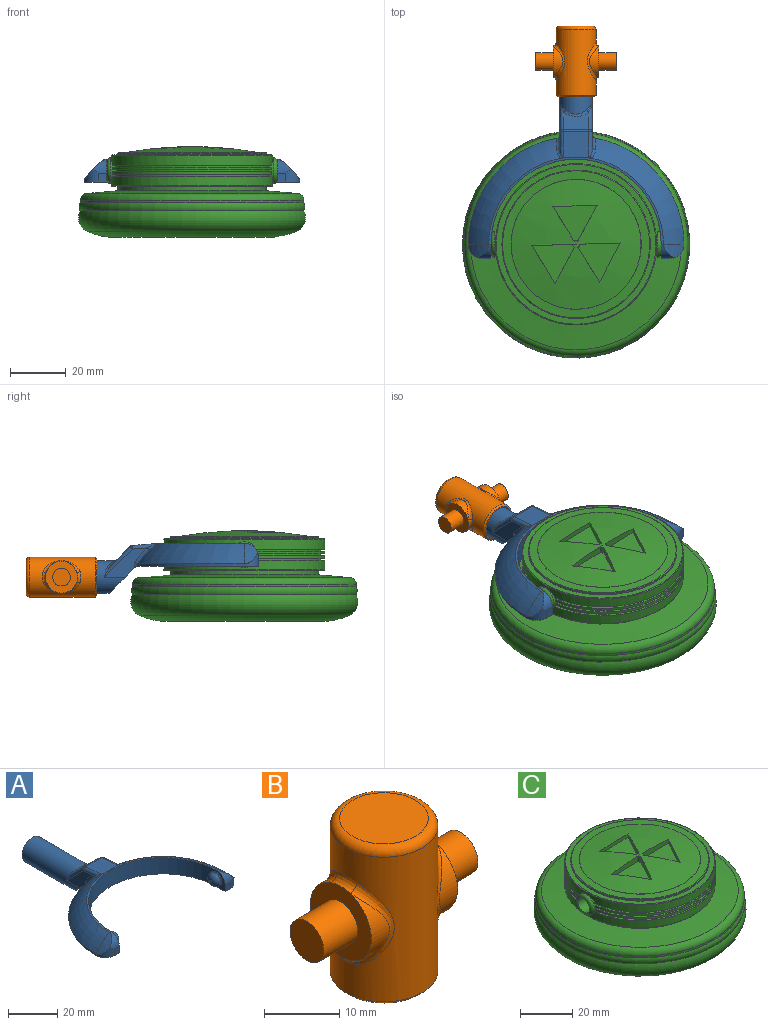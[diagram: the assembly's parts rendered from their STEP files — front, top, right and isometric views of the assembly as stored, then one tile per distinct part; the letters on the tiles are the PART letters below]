
ASSEMBLY  parts=3 mates=2
PART A: 48 faces, bbox 77.3x80.8x18.2 mm
  f0: plane 11.99x9.83mm, normal (0,-0.71,-0.71), area 141.5mm2, adj f1,f2,f9,f30,f43,f46
  f1: plane 15.39x10.49mm, normal (-1,0,0), area 63.5mm2, adj f0,f30,f32,f36,f46,f47
  f2: plane 15.39x10.49mm, normal (1,0,0), area 63.5mm2, adj f0,f30,f34,f39,f43,f44
  f3: plane 9.14x6.37mm, normal (0,0.71,0.71), area 67.6mm2, adj f35,f36,f39,f40
  f4: cylinder r=38.61mm len=37.99mm, axis (0,0,-1), area 42.6mm2, adj f6,f9,f17,f46,f47
  f5: torus R=19.3mm, axis (0,0,-1), area 507.8mm2, adj f10,f11,f12,f29,f42,f44
  f6: torus R=19.3mm, axis (0,0,-1), area 507.8mm2, adj f4,f11,f15,f28,f45,f47
  f7: cylinder r=30.48mm len=60.96mm, axis (0,0,-1), area 746.6mm2, adj f8,f9,f11,f14,f21,f24
  f8: plane 8.13x5.08mm, normal (-1,0,0), area 19.9mm2, adj f7,f9,f13,f19,f24
  f9: plane 77.22x43.73mm, normal (0,0,-1), area 956.2mm2, adj f0,f4,f7,f8,f10,f13,f14,f16
  f10: cylinder r=38.61mm len=37.99mm, axis (0,0,-1), area 42.6mm2, adj f5,f9,f20,f43,f44
  f11: plane 62.55x30.95mm, normal (0,0,1), area 75mm2, adj f5,f6,f7,f18,f19,f27
  f12: cylinder r=22.71mm len=7.33mm, axis (0,1,0), area 24.8mm2, adj f5,f19,f20
  f13: plane 3.05x3.05mm, normal (0,-1,0), area 9.3mm2, adj f8,f9,f19,f20
  f14: plane 8.13x5.08mm, normal (1,0,0), area 19.9mm2, adj f7,f9,f16,f18,f21
  f15: cylinder r=22.71mm len=7.33mm, axis (0,1,0), area 24.8mm2, adj f6,f17,f18
  f16: plane 3.05x3.05mm, normal (0,-1,0), area 9.3mm2, adj f9,f14,f17,f18
  f17: cylinder r=5.08mm len=5.08mm, axis (0,0,-1), area 21.9mm2, adj f4,f9,f15,f16,f18
  f18: cylinder r=5.08mm len=5.08mm, axis (-1,0,0), area 21.9mm2, adj f11,f14,f15,f16,f17
  f19: cylinder r=5.08mm len=5.08mm, axis (-1,0,0), area 21.9mm2, adj f8,f11,f12,f13,f20
  f20: cylinder r=5.08mm len=5.08mm, axis (0,0,-1), area 21.9mm2, adj f9,f10,f12,f13,f19
  f21: cylinder r=3.17mm len=6.35mm, axis (-1,0,0), area 12.7mm2, adj f7,f14,f23
  f22: plane 1.27x1.27mm, normal (1,0,0), area 1.3mm2, adj f23
  f23: torus R=0.64mm, axis (1,0,0), area 56.5mm2, adj f21,f22
  f24: cylinder r=3.17mm len=6.35mm, axis (1,0,0), area 12.7mm2, adj f7,f8,f26
  f25: plane 1.27x1.27mm, normal (-1,0,0), area 1.3mm2, adj f26
  f26: torus R=0.64mm, axis (-1,0,0), area 56.5mm2, adj f24,f25
  f27: plane 9.86x9.36mm, normal (0,0.09,1), area 85.6mm2, adj f11,f28,f29,f32,f34,f35,f42,f45
  f28: plane 1.04x0.17mm, normal (0,-1,0), area 0mm2, adj f6,f27,f45
  f29: plane 1.04x0.17mm, normal (0,-1,0), area 0mm2, adj f5,f27,f42
  f30: cylinder r=5.84mm len=33.01mm, axis (0,-1,0), area 1029.7mm2, adj f0,f1,f2,f31,f38,f40,f41
  f31: plane 11.68x11.68mm, normal (0,1,0), area 107.2mm2, adj f30
  f32: cylinder r=1.27mm len=9.13mm, axis (0,-1,0.09), area 14.4mm2, adj f1,f27,f33,f45
  f33: sphere r=1.27mm, area 1.5mm2, adj f32,f35,f36
  f34: cylinder r=1.27mm len=9.13mm, axis (0,1,-0.09), area 14.4mm2, adj f2,f27,f37,f42
  f35: cylinder r=1.27mm len=9.14mm, axis (-1,0,0), area 8.1mm2, adj f3,f27,f33,f37
  f36: cylinder r=1.27mm len=10.91mm, axis (0,-0.71,0.71), area 23.1mm2, adj f1,f3,f33,f38
  f37: sphere r=1.27mm, area 1.5mm2, adj f34,f35,f39
  f38: bspline ~4.55x2.75mm, area 2.3mm2, adj f30,f36,f40
  f39: cylinder r=1.27mm len=10.91mm, axis (0,0.71,-0.71), area 23.1mm2, adj f2,f3,f37,f41
  f40: bspline ~9.14x2.56mm, area 10.7mm2, adj f3,f30,f38,f41
  f41: bspline ~5.23x3.53mm, area 2.3mm2, adj f30,f39,f40
  f42: bspline ~4.62x3.14mm, area 5.2mm2, adj f5,f27,f29,f34,f44
  f43: cylinder r=1.27mm len=1.74mm, axis (0,0,-1), area 1.9mm2, adj f0,f2,f9,f10,f44
  f44: bspline ~8.6x7.86mm, area 11.9mm2, adj f2,f5,f10,f42,f43
  f45: bspline ~4.62x3.14mm, area 5.2mm2, adj f6,f27,f28,f32,f47
  f46: cylinder r=1.27mm len=1.74mm, axis (0,0,-1), area 1.9mm2, adj f0,f1,f4,f9,f47
  f47: bspline ~8.6x7.86mm, area 11.9mm2, adj f1,f4,f6,f45,f46
PART B: 25 faces, bbox 28.9x15.5x25.4 mm
  f0: cylinder r=5.71mm len=10.81mm, axis (-1,0,0), area 26.2mm2, adj f5,f15
  f1: cylinder r=5.71mm len=10.81mm, axis (-1,0,0), area 26.2mm2, adj f8,f11
  f2: cylinder r=7.14mm len=23.5mm, axis (0,0,-1), area 763.2mm2, adj f9,f10,f11,f12,f13,f14,f15,f16
  f3: plane 11.75x11.75mm, normal (0,0,1), area 108.4mm2, adj f17
  f4: plane 13.02x13.02mm, normal (0,0,-1), area 16.3mm2, adj f22,f24
  f5: plane 11.46x11.46mm, normal (1,0,0), area 70.9mm2, adj f0,f6,f13,f16,f18
  f6: cylinder r=5.71mm len=10.81mm, axis (-1,0,0), area 26.2mm2, adj f5,f14
  f7: cylinder r=5.71mm len=10.81mm, axis (-1,0,0), area 26.2mm2, adj f8,f10
  f8: plane 11.46x11.46mm, normal (-1,0,0), area 70.9mm2, adj f1,f7,f9,f12,f20
  f9: bspline ~4.64x1.73mm, area 6.5mm2, adj f2,f8,f10,f11
  f10: bspline ~13.62x4.91mm, area 20.7mm2, adj f2,f7,f9,f12
  f11: bspline ~13.6x4.87mm, area 20.7mm2, adj f1,f2,f9,f12
  f12: bspline ~4.64x1.73mm, area 6.5mm2, adj f2,f8,f10,f11
  f13: bspline ~4.64x1.73mm, area 6.5mm2, adj f2,f5,f14,f15
  f14: bspline ~13.62x4.91mm, area 20.7mm2, adj f2,f6,f13,f16
  f15: bspline ~13.6x4.87mm, area 20.7mm2, adj f0,f2,f13,f16
  f16: bspline ~4.64x1.73mm, area 6.5mm2, adj f2,f5,f14,f15
  f17: torus R=5.87mm, axis (0,0,1), area 83.8mm2, adj f2,f3
  f18: cylinder r=3.17mm len=6.35mm, axis (-1,0,0), area 126.7mm2, adj f5,f19
  f19: plane 6.35x6.35mm, normal (1,0,0), area 31.7mm2, adj f18
  f20: cylinder r=3.17mm len=6.35mm, axis (1,0,0), area 126.7mm2, adj f8,f21
  f21: plane 6.35x6.35mm, normal (-1,0,0), area 31.7mm2, adj f20
  f22: cylinder r=6.1mm len=22.86mm, axis (0,0,-1), area 875.6mm2, adj f4,f23
  f23: plane 12.19x12.19mm, normal (0,0,-1), area 116.7mm2, adj f22
  f24: cone r=7.14mm half-angle=45deg, axis (0,0,1), area 38.5mm2, adj f2,f4
PART C: 64 faces, bbox 96.2x96.2x32.5 mm
  f0: cylinder r=28.87mm len=57.73mm, axis (0,0,-1), area 595.6mm2, adj f1,f2,f54,f55,f60
  f1: plane 57.13x24.71mm, normal (0,0,1), area 102.9mm2, adj f0,f3,f54,f55
  f2: plane 57.13x24.71mm, normal (0,0,1), area 102.9mm2, adj f0,f4,f54,f55
  f3: cylinder r=27.59mm len=54.54mm, axis (0,0,-1), area 49.6mm2, adj f1,f6,f54,f55
  f4: cylinder r=27.59mm len=54.54mm, axis (0,0,-1), area 49.6mm2, adj f2,f5,f54,f55
  f5: plane 57.06x24.48mm, normal (0,0,-1), area 102.3mm2, adj f4,f8,f54,f55
  f6: plane 57.06x24.48mm, normal (0,0,-1), area 102.3mm2, adj f3,f7,f54,f55
  f7: cylinder r=28.87mm len=57.06mm, axis (0,0,-1), area 77.8mm2, adj f6,f11,f54,f55
  f8: cylinder r=28.87mm len=57.06mm, axis (0,0,-1), area 77.8mm2, adj f5,f12,f54,f55
  f9: plane 57.01x24.31mm, normal (0,0,-1), area 101.8mm2, adj f14,f16,f54,f55
  f10: plane 57.01x24.31mm, normal (0,0,-1), area 101.8mm2, adj f13,f15,f54,f55
  f11: plane 57.01x24.31mm, normal (0,0,1), area 101.8mm2, adj f7,f13,f54,f55
  f12: plane 57.01x24.31mm, normal (0,0,1), area 101.8mm2, adj f8,f14,f54,f55
  f13: cylinder r=27.59mm len=54.41mm, axis (0,0,-1), area 49.2mm2, adj f10,f11,f54,f55
  f14: cylinder r=27.59mm len=54.41mm, axis (0,0,-1), area 49.2mm2, adj f9,f12,f54,f55
  f15: cylinder r=28.87mm len=57.06mm, axis (0,0,-1), area 77.9mm2, adj f10,f19,f54,f55
  f16: cylinder r=28.87mm len=57.06mm, axis (0,0,-1), area 77.9mm2, adj f9,f20,f54,f55
  f17: plane 57.13x24.71mm, normal (0,0,-1), area 102.9mm2, adj f22,f23,f54,f55
  f18: plane 57.13x24.71mm, normal (0,0,-1), area 102.9mm2, adj f21,f23,f54,f55
  f19: plane 57.06x24.48mm, normal (0,0,1), area 102.3mm2, adj f15,f21,f54,f55
  f20: plane 57.06x24.48mm, normal (0,0,1), area 102.3mm2, adj f16,f22,f54,f55
  f21: cylinder r=27.59mm len=54.54mm, axis (0,0,-1), area 49.6mm2, adj f18,f19,f54,f55
  f22: cylinder r=27.59mm len=54.54mm, axis (0,0,-1), area 49.6mm2, adj f17,f20,f54,f55
  f23: cylinder r=28.87mm len=57.73mm, axis (0,0,-1), area 595.8mm2, adj f17,f18,f54,f55,f61
  f24: sphere r=135.39mm, area 1385.3mm2, adj f38,f39,f40,f41,f43,f44,f45,f46
  f25: plane 39.33x39.33mm, normal (0,0,-1), area 1214.6mm2, adj f26
  f26: torus R=20.12mm, axis (0,0,-1), area 1429.3mm2, adj f25,f27
  f27: torus R=27.74mm, axis (0,0,-1), area 3542.1mm2, adj f26,f28
  f28: torus R=35.36mm, axis (0,0,-1), area 2180.1mm2, adj f27,f29
  f29: torus R=37.35mm, axis (0,0,-1), area 734.6mm2, adj f28,f30
  f30: cylinder r=40.06mm len=80.11mm, axis (0,0,-1), area 213.3mm2, adj f29,f34
  f31: cone r=26.57mm half-angle=85deg, axis (0,0,-1), area 2265mm2, adj f32,f34
  f32: cylinder r=26.57mm len=53.14mm, axis (0,0,-1), area 265mm2, adj f31,f33
  f33: plane 57.23x57.23mm, normal (0,0,-1), area 354.5mm2, adj f32,f60
  f34: torus R=37.52mm, axis (0,0,1), area 928.6mm2, adj f30,f31
  f35: cone r=26.57mm half-angle=87deg, axis (0,0,-1), area 475.4mm2, adj f62,f63
  f36: cylinder r=26.57mm len=53.14mm, axis (0,0,-1), area 92.3mm2, adj f37,f62
  f37: plane 57.23x57.23mm, normal (0,0,1), area 354.5mm2, adj f36,f61
  f38: cylinder r=1.27mm len=2.53mm, axis (0,0,1), area 3.4mm2, adj f24,f39,f41,f42
  f39: plane 12.43x7.68mm, normal (0.85,0.53,0), area 32.2mm2, adj f24,f38,f40,f42
  f40: plane 13.98x7.52mm, normal (-0.88,0.47,0), area 28mm2, adj f24,f39,f41,f42
  f41: plane 14.6x2.53mm, normal (0.03,-1,0), area 32.2mm2, adj f24,f38,f40,f42
  f42: plane 15.2x13.98mm, normal (0,0,1), area 108.3mm2, adj f38,f39,f40,f41
  f43: plane 12.86x6.92mm, normal (-0.88,0.47,0), area 32.2mm2, adj f24,f44,f46,f47
  f44: cylinder r=1.27mm len=2.53mm, axis (0,0,1), area 3.4mm2, adj f24,f43,f45,f47
  f45: plane 14.6x2.53mm, normal (0.03,-1,0), area 32.2mm2, adj f24,f44,f46,f47
  f46: plane 13.51x8.34mm, normal (0.85,0.53,0), area 28mm2, adj f24,f43,f45,f47
  f47: plane 15.27x13.94mm, normal (0,0,1), area 108.3mm2, adj f43,f44,f45,f46
  f48: cylinder r=1.27mm len=2.53mm, axis (0,0,1), area 3.4mm2, adj f24,f49,f51,f52
  f49: plane 12.86x6.92mm, normal (-0.88,0.47,0), area 32.2mm2, adj f24,f48,f50,f52
  f50: plane 15.87x1.84mm, normal (0.03,-1,0), area 28mm2, adj f24,f49,f51,f52
  f51: plane 12.43x7.68mm, normal (0.85,0.53,0), area 32.2mm2, adj f24,f48,f50,f52
  f52: plane 15.87x12.9mm, normal (0,0,1), area 108.3mm2, adj f48,f49,f50,f51
  f53: plane 6.6x6.6mm, normal (1,0,0), area 2.6mm2, adj f58,f59
  f54: cylinder r=4.57mm len=9.14mm, axis (-1,0,0), area 20.2mm2, adj f0,f1,f2,f3,f4,f5,f6,f7
  f55: cylinder r=4.57mm len=9.14mm, axis (-1,0,0), area 20.2mm2, adj f0,f1,f2,f3,f4,f5,f6,f7
  f56: plane 6.6x6.6mm, normal (-1,0,0), area 2.6mm2, adj f57,f59
  f57: torus R=3.3mm, axis (1,0,0), area 51.5mm2, adj f55,f56
  f58: torus R=3.3mm, axis (1,0,0), area 51.5mm2, adj f53,f54
  f59: cylinder r=3.17mm len=60.96mm, axis (1,0,0), area 1216.1mm2, adj f53,f56
  f60: torus R=28.61mm, axis (0,0,1), area 72.1mm2, adj f0,f33
  f61: torus R=28.61mm, axis (0,0,-1), area 72.1mm2, adj f23,f37
  f62: torus R=26.31mm, axis (0,0,1), area 64.2mm2, adj f35,f36
  f63: torus R=23.29mm, axis (0,0,1), area 4.5mm2, adj f24,f35
PLACE A t=(32.34,27.52,20.85)mm
PLACE B rot(axis=(-1,0,0),90deg) t=(32.34,80.3,16.88)mm
PLACE C t=(32.34,27.52,33.52)mm
MATE revolute A.f24 <-> C.f54  axis (-1,0,0) through (62.82,27.52,24.92)mm
MATE revolute B.f2 <-> A.f30  axis (0,-1,0) through (32.34,103.16,16.88)mm
